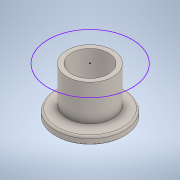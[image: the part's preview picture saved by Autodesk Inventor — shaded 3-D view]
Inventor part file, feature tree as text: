
AUTODESK INVENTOR PART (.ipt)
format: ipt  version: 2021 (Build 250183000, 183)  size: 154,112 bytes
history: native  units: in
note: dims shown in document units (in); Inventor stores cm internally (conversion verified against a paired STEP export)
features: sketch x1, chamfer x1
ambient origin geometry x8: Origin, YZ Plane, XZ Plane, XY Plane, X Axis, Y Axis, Z Axis, Center Point
bodies: Solid1 (feature_tree)
feature tree (2):
  sketch  "Sketch1"
  chamfer  "Chamfer2"  [1 undecoded]
note: 1 required parameter value undecoded (feature->parameter linkage not recoverable at this tier; creation-order binding heuristic only, values carry confidence <= 0.55)
